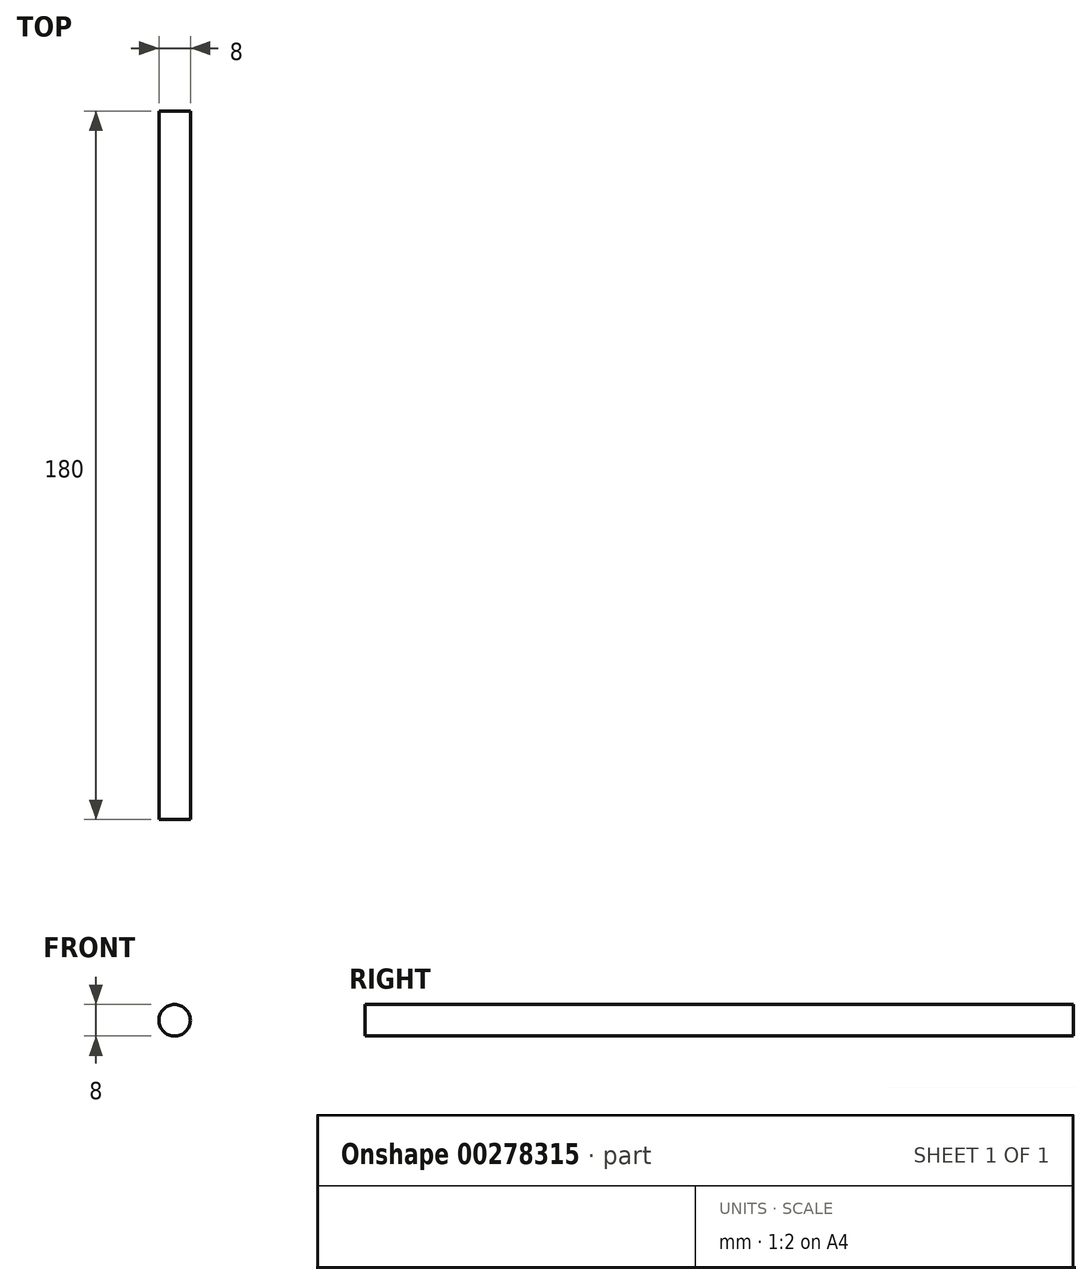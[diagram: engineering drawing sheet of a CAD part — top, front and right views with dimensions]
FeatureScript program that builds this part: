
annotation { "Feature Type Name" : "Feature", "Feature Type Description" : "" }
export const myFeature = defineFeature(function(context is Context, id is Id, definition is map)
    precondition{}
    {
        {
            var Q0;
            Q0=qCreatedBy(makeId("Front.planeOp"),FACE);
            var sketch = newSketch(context, id + "F0", { "sketchPlane" : qUnion([Q0])});
            skCircle(sketch, "E0", {"center": v(0, 0) * mm, "radius": 4 * mm});
            skSolve(sketch);
        }
        {
            var Q0;
            Q0=makeQuery(id+"F0.imprint","IMPRINT",FACE,{"disambiguationData":[TD([[makeQuery(id+"F0.imprint","IMPRINT",EDGE,{"derivedFrom":sQuery(id+"F0.wireOp",EDGE,"E0")}),1.0]])]});
            extrude(context, id + "F1", {"entities" : qUnion([Q0]), "endBound" : BoundingType.SYMMETRIC, "depth" : 180 * mm});
        }
    });
